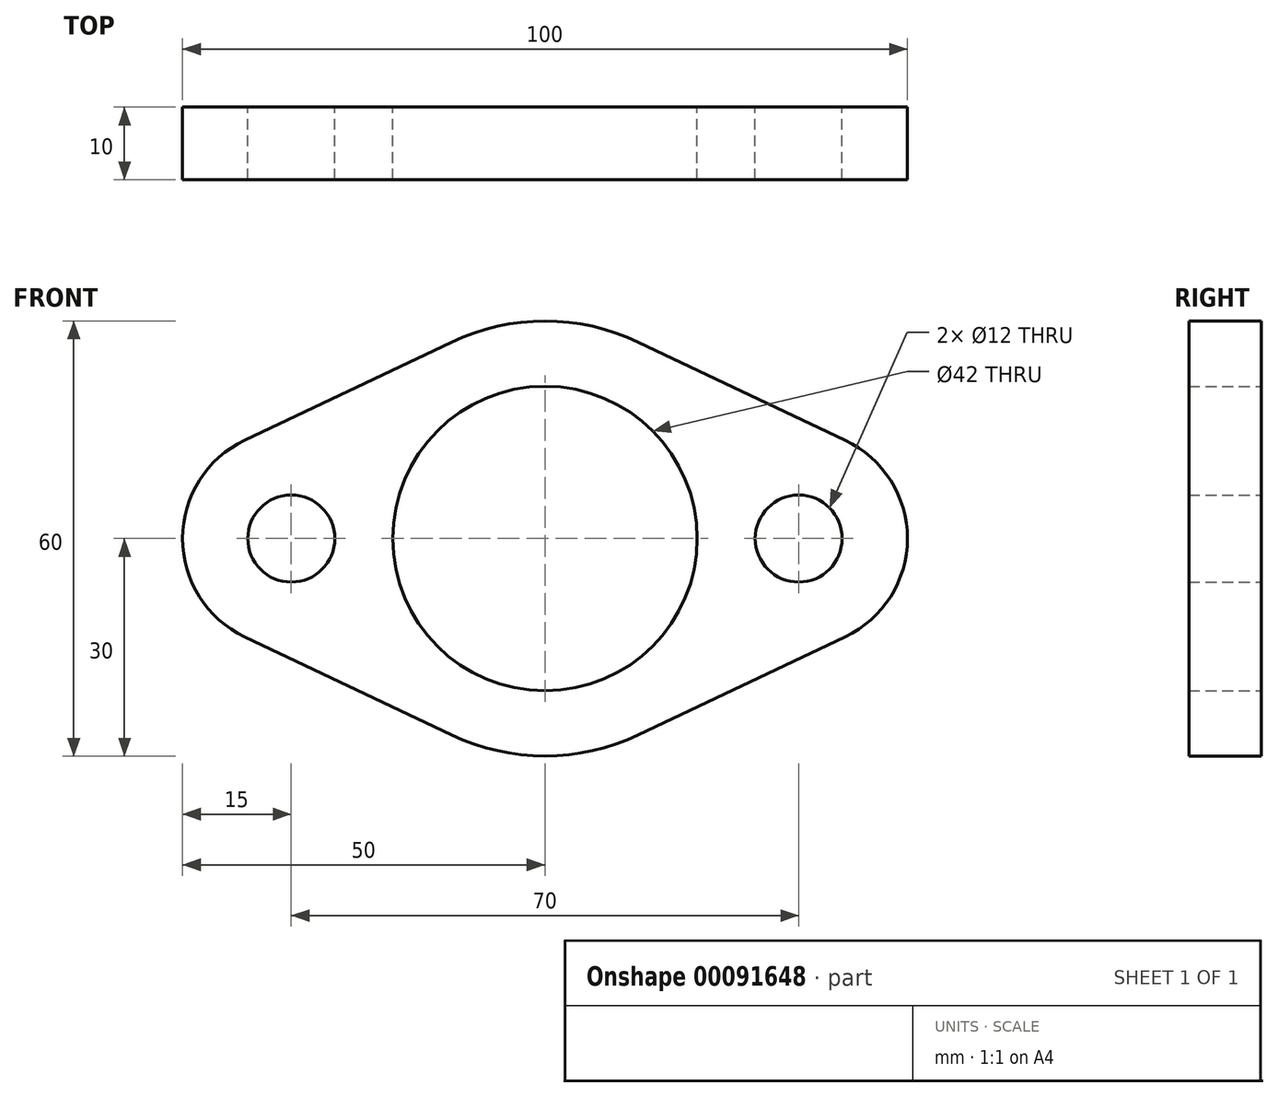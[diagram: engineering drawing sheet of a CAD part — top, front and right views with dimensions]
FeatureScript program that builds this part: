
annotation { "Feature Type Name" : "Feature", "Feature Type Description" : "" }
export const myFeature = defineFeature(function(context is Context, id is Id, definition is map)
    precondition{}
    {
        {
            var Q0;
            Q0=qCreatedBy(makeId("Front.planeOp"),FACE);
            var sketch = newSketch(context, id + "F0", { "sketchPlane" : qUnion([Q0])});
            skArc(sketch, "E0", {"start": v(12.86, 27.1) * mm, "mid": v(6.59, 29.27) * mm, "end": v(0, 30) * mm});
            skLineSegment(sketch, "E1", {"start": v(12.86, 27.1) * mm, "end": v(41.43, 13.55) * mm});
            skLineSegment(sketch, "E2", {"start": v(-56.6, 0) * mm, "end": v(66.45, 0) * mm, "construction": true});
            skLineSegment(sketch, "E3", {"start": v(0, 49.53) * mm, "end": v(0, -49.22) * mm, "construction": true});
            skArc(sketch, "E4.trimOffspring", {"start": v(50, 0) * mm, "mid": v(47.68, 8.02) * mm, "end": v(41.43, 13.55) * mm});
            skLineSegment(sketch, "E5.MirrorCS", {"start": v(56.6, 0) * mm, "end": v(-66.45, 0) * mm, "construction": true});
            skArc(sketch, "E6", {"start": v(21, 0) * mm, "mid": v(14.85, 14.85) * mm, "end": v(0, 21) * mm});
            skArc(sketch, "E7.MirrorCS", {"start": v(-12.86, 27.1) * mm, "mid": v(-6.59, 29.27) * mm, "end": v(0, 30) * mm});
            skLineSegment(sketch, "E8.MirrorCS", {"start": v(-12.86, 27.1) * mm, "end": v(-41.43, 13.55) * mm});
            skArc(sketch, "E9.MirrorCS", {"start": v(-50, 0) * mm, "mid": v(-47.68, 8.02) * mm, "end": v(-41.43, 13.55) * mm});
            skArc(sketch, "E10.MirrorCS", {"start": v(-21, 0) * mm, "mid": v(-14.85, 14.85) * mm, "end": v(0, 21) * mm});
            skArc(sketch, "E11.MirrorCS", {"start": v(21, 0) * mm, "mid": v(14.85, -14.85) * mm, "end": v(0, -21) * mm});
            skArc(sketch, "E12.MirrorCS", {"start": v(-21, 0) * mm, "mid": v(-14.85, -14.85) * mm, "end": v(0, -21) * mm});
            skArc(sketch, "E13.MirrorCS", {"start": v(-50, 0) * mm, "mid": v(-47.68, -8.02) * mm, "end": v(-41.43, -13.55) * mm});
            skLineSegment(sketch, "E14.MirrorCS", {"start": v(-12.86, -27.1) * mm, "end": v(-41.43, -13.55) * mm});
            skArc(sketch, "E15.MirrorCS", {"start": v(-12.86, -27.1) * mm, "mid": v(-6.59, -29.27) * mm, "end": v(0, -30) * mm});
            skArc(sketch, "E16.MirrorCS", {"start": v(12.86, -27.1) * mm, "mid": v(6.59, -29.27) * mm, "end": v(0, -30) * mm});
            skLineSegment(sketch, "E17.MirrorCS", {"start": v(12.86, -27.1) * mm, "end": v(41.43, -13.55) * mm});
            skArc(sketch, "E18.MirrorCS", {"start": v(50, 0) * mm, "mid": v(47.68, -8.02) * mm, "end": v(41.43, -13.55) * mm});
            skCircle(sketch, "E19", {"center": v(35, 0) * mm, "radius": 6 * mm});
            skCircle(sketch, "E20", {"center": v(-35, 0) * mm, "radius": 6 * mm});
            skSolve(sketch);
        }
        {
            var Q0;
            Q0=makeQuery(id+"F0.imprint","IMPRINT",FACE,{"disambiguationData":[TD([[makeQuery(id+"F0.imprint","IMPRINT",EDGE,{"derivedFrom":sQuery(id+"F0.wireOp",EDGE,"E0")}),1.0]])]});
            extrude(context, id + "F1", {"entities" : qUnion([Q0]), "depth" : 10 * mm});
        }
    });
